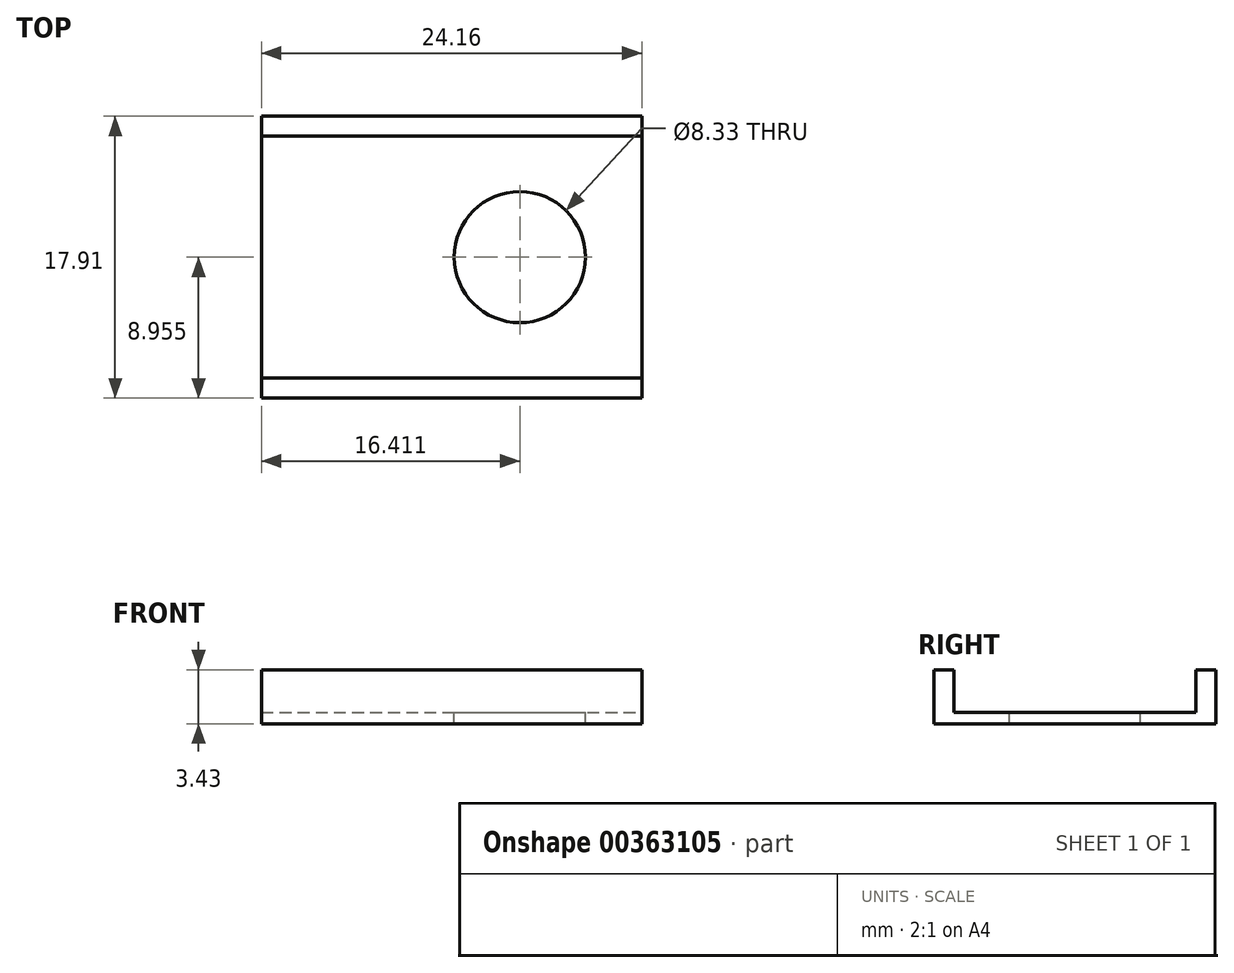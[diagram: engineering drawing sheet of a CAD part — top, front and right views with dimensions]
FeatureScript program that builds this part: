
annotation { "Feature Type Name" : "Feature", "Feature Type Description" : "" }
export const myFeature = defineFeature(function(context is Context, id is Id, definition is map)
    precondition{}
    {
        {
            var Q0;
            Q0=qCreatedBy(makeId("Top.planeOp"),FACE);
            var sketch = newSketch(context, id + "F0", { "sketchPlane" : qUnion([Q0])});
            skLineSegment(sketch, "E0.bottom", {"start": v(-52.08, 35.53) * mm, "end": v(-27.93, 35.53) * mm});
            skLineSegment(sketch, "E0.top", {"start": v(-52.08, 17.62) * mm, "end": v(-27.93, 17.62) * mm});
            skLineSegment(sketch, "E0.left", {"start": v(-52.08, 35.53) * mm, "end": v(-52.08, 17.62) * mm});
            skLineSegment(sketch, "E0.right", {"start": v(-27.93, 35.53) * mm, "end": v(-27.93, 17.62) * mm});
            skSolve(sketch);
        }
        {
            var Q0;
            Q0=makeQuery(id+"F0.imprint","IMPRINT",FACE,{"disambiguationData":[TD([[makeQuery(id+"F0.imprint","IMPRINT",EDGE,{"derivedFrom":sQuery(id+"F0.wireOp",EDGE,"E0.bottom")}),-1.0]])]});
            extrude(context, id + "F1", {"entities" : qUnion([Q0]), "depth" : 4.57 * mm});
        }
        {
            var Q0;
            Q0=qCreatedBy(makeId("Top.planeOp"),FACE);
            var sketch = newSketch(context, id + "F2", { "sketchPlane" : qUnion([Q0])});
            skLineSegment(sketch, "E1.bottom", {"start": v(-52.09, 17.62) * mm, "end": v(-27.93, 17.62) * mm});
            skLineSegment(sketch, "E1.top", {"start": v(-52.09, 35.53) * mm, "end": v(-27.93, 35.53) * mm});
            skLineSegment(sketch, "E1.left", {"start": v(-52.09, 17.62) * mm, "end": v(-52.09, 35.53) * mm});
            skLineSegment(sketch, "E1.right", {"start": v(-27.93, 17.62) * mm, "end": v(-27.93, 35.53) * mm});
            skSolve(sketch);
        }
        {
            var Q0;
            Q0=qSketchRegion(id+"F2",true);
            extrude(context, id + "F3", {"entities" : qUnion([Q0]), "operationType" : NewBodyOperationType.ADD, "oppositeDirection" : true, "depth" : 3.43 * mm});
        }
        {
            var Q0;
            Q0=qCreatedBy(makeId("Right.planeOp"),FACE);
            var sketch = newSketch(context, id + "F4", { "sketchPlane" : qUnion([Q0])});
            skLineSegment(sketch, "E2.bottom", {"start": v(18.9, 3.3) * mm, "end": v(34.26, 3.3) * mm});
            skLineSegment(sketch, "E2.top", {"start": v(18.9, -2.72) * mm, "end": v(34.26, -2.72) * mm});
            skLineSegment(sketch, "E2.left", {"start": v(18.9, 3.3) * mm, "end": v(18.9, -2.72) * mm});
            skLineSegment(sketch, "E2.right", {"start": v(34.26, 3.3) * mm, "end": v(34.26, -2.72) * mm});
            skSolve(sketch);
        }
        {
            var Q0;
            Q0=qSketchRegion(id+"F4",true);
            extrude(context, id + "F5", {"entities" : qUnion([Q0]), "operationType" : NewBodyOperationType.REMOVE, "endBound" : BoundingType.THROUGH_ALL, "oppositeDirection" : true, "depth" : 25.4 * mm});
        }
        {
            var Q0;
            Q0=qCreatedBy(makeId("Top.planeOp"),FACE);
            var sketch = newSketch(context, id + "F6", { "sketchPlane" : qUnion([Q0])});
            skCircle(sketch, "E3", {"center": v(-35.68, 26.58) * mm, "radius": 4.17 * mm});
            skLineSegment(sketch, "E4", {"start": v(-35.68, 17.62) * mm, "end": v(-35.68, 35.53) * mm});
            skLineSegment(sketch, "E5", {"start": v(-52.09, 26.58) * mm, "end": v(-27.93, 26.58) * mm});
            skSolve(sketch);
        }
        {
            var Q0;
            Q0=qSketchRegion(id+"F6",true);
            extrude(context, id + "F7", {"entities" : qUnion([Q0]), "operationType" : NewBodyOperationType.REMOVE, "oppositeDirection" : true, "depth" : 25.4 * mm});
        }
        {
            var Q0;
            Q0=qCreatedBy(makeId("Right.planeOp"),FACE);
            var sketch = newSketch(context, id + "F8", { "sketchPlane" : qUnion([Q0])});
            skLineSegment(sketch, "E6.bottom", {"start": v(17.1, 5.1) * mm, "end": v(37.32, 5.1) * mm});
            skLineSegment(sketch, "E6.top", {"start": v(17.1, 0) * mm, "end": v(37.32, 0) * mm});
            skLineSegment(sketch, "E6.left", {"start": v(17.1, 5.1) * mm, "end": v(17.1, 0) * mm});
            skLineSegment(sketch, "E6.right", {"start": v(37.32, 5.1) * mm, "end": v(37.32, 0) * mm});
            skSolve(sketch);
        }
        {
            var Q0;
            Q0 = qSketchRegion(id + "F8", true);
            extrude(context, id + "F9", {"entities" : qUnion([Q0]), "operationType" : NewBodyOperationType.REMOVE, "endBound" : BoundingType.THROUGH_ALL, "oppositeDirection" : true, "depth" : 25.4 * mm});
        }
    });
